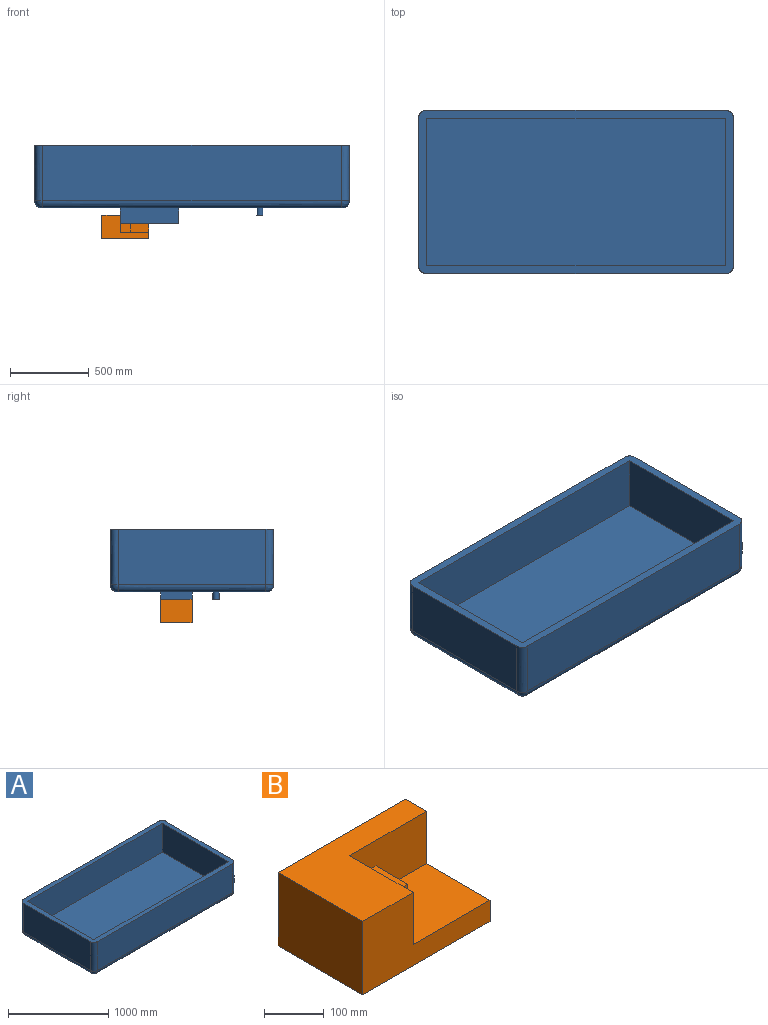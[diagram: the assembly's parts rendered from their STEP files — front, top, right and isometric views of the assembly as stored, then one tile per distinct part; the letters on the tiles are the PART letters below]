
ASSEMBLY  parts=2 mates=3
PART A: 30 faces, bbox 2134.8x1096x521.5 mm
  f0: plane 1900x936.19mm, normal (0,0,-1), area 1704235.5mm2, adj f12,f15,f16,f18,f23,f25,f26,f27
  f1: plane 2001.45x1037.65mm, normal (0,0,1), area 292027.6mm2, adj f2,f3,f4,f5,f6,f7,f8,f9
  f2: plane 1900x350mm, normal (0,1,0), area 665000mm2, adj f1,f11,f14,f15
  f3: plane 936.19x350mm, normal (-1,0,0), area 327667.8mm2, adj f1,f11,f12,f13
  f4: plane 1900x350mm, normal (0,-1,0), area 665000mm2, adj f1,f13,f16,f17
  f5: plane 936.19x350mm, normal (1,0,0), area 327667.8mm2, adj f1,f14,f17,f18
  f6: plane 1900x350mm, normal (0,-1,0), area 665000mm2, adj f1,f7,f9,f10
  f7: plane 936.19x350mm, normal (1,0,0), area 327667.8mm2, adj f1,f6,f8,f10
  f8: plane 1900x350mm, normal (0,1,0), area 665000mm2, adj f1,f7,f9,f10
  f9: plane 936.19x350mm, normal (-1,0,0), area 327667.8mm2, adj f1,f6,f8,f10
  f10: plane 1900x936.19mm, normal (0,0,1), area 1778768.3mm2, adj f6,f7,f8,f9
  f11: bspline ~424.44x50mm, area 28458.9mm2, adj f1,f2,f3,f19
  f12: bspline ~1094.56x50mm, area 76122.7mm2, adj f0,f3,f19,f20
  f13: bspline ~424.44x50mm, area 28458.9mm2, adj f1,f3,f4,f20
  f14: bspline ~424.44x50mm, area 28458.9mm2, adj f1,f2,f5,f21
  f15: bspline ~2133.33x50mm, area 154490.6mm2, adj f0,f2,f19,f21
  f16: bspline ~2133.33x50mm, area 154490.6mm2, adj f0,f4,f20,f22
  f17: bspline ~424.44x50mm, area 28458.9mm2, adj f1,f4,f5,f22
  f18: bspline ~1094.56x50mm, area 76122.7mm2, adj f0,f5,f21,f22
  f19: bspline ~79.36x79.2mm, area 2973.9mm2, adj f11,f12,f15
  f20: bspline ~79.36x79.2mm, area 2973.9mm2, adj f12,f13,f16
  f21: bspline ~79.36x79.2mm, area 2973.9mm2, adj f14,f15,f18
  f22: bspline ~79.36x79.2mm, area 2973.9mm2, adj f16,f17,f18
  f23: cylinder r=20mm len=50mm, axis (0,0,1), area 6283.2mm2, adj f0,f24
  f24: plane 40x40mm, normal (0,0,-1), area 1256.6mm2, adj f23
  f25: plane 198.3x100mm, normal (-1,0,0), area 19829.8mm2, adj f0,f26,f28,f29
  f26: plane 369.53x100mm, normal (0,1,0), area 36952.6mm2, adj f0,f25,f27,f29
  f27: plane 198.3x100mm, normal (1,0,0), area 19829.8mm2, adj f0,f26,f28,f29
  f28: plane 369.53x100mm, normal (0,-1,0), area 36952.6mm2, adj f0,f25,f27,f29
  f29: plane 369.53x198.3mm, normal (0,0,-1), area 73276.2mm2, adj f25,f26,f27,f28
PART B: 12 faces, bbox 300x200x150 mm
  f0: plane 150x106.49mm, normal (1,0,0), area 11899.6mm2, adj f1,f2,f4,f8,f10,f11
  f1: plane 181.25x106.49mm, normal (0,-1,0), area 15910.9mm2, adj f0,f3,f4,f8,f9,f10
  f2: plane 300x150mm, normal (0,-1,0), area 25698.3mm2, adj f0,f3,f4,f6,f7,f8
  f3: plane 200x150mm, normal (1,0,0), area 14025.9mm2, adj f1,f2,f4,f5,f7,f8
  f4: plane 300x200mm, normal (0,0,1), area 32813mm2, adj f0,f1,f2,f3,f5,f6
  f5: plane 300x150mm, normal (0,1,0), area 45000mm2, adj f3,f4,f6,f7
  f6: plane 200x150mm, normal (-1,0,0), area 30000mm2, adj f2,f4,f5,f7
  f7: plane 300x200mm, normal (0,0,-1), area 60000mm2, adj f2,f3,f5,f6
  f8: plane 181.25x150mm, normal (0,0,1), area 22505.8mm2, adj f0,f1,f2,f3,f9,f11
  f9: plane 75x54.33mm, normal (1,0,0), area 4074.5mm2, adj f1,f8,f10,f11
  f10: plane 75x62.42mm, normal (0,0,1), area 4681.2mm2, adj f0,f1,f9,f11
  f11: plane 62.42x54.33mm, normal (0,-1,0), area 3390.9mm2, adj f0,f8,f9,f10
PLACE A at identity fixed
PLACE B t=(-509.9,198.1,-197.83)mm
MATE planar A.f25 <-> B.f0  axis (-1,0,0) through (-454.75,17.99,-50)mm
MATE planar B.f10 <-> A.f29  axis (0,0,1) through (-423.54,130.49,-100)mm
MATE planar B.f1 <-> B.f3  axis (0,-1,0) through (-351.46,167.99,-95.52)mm
